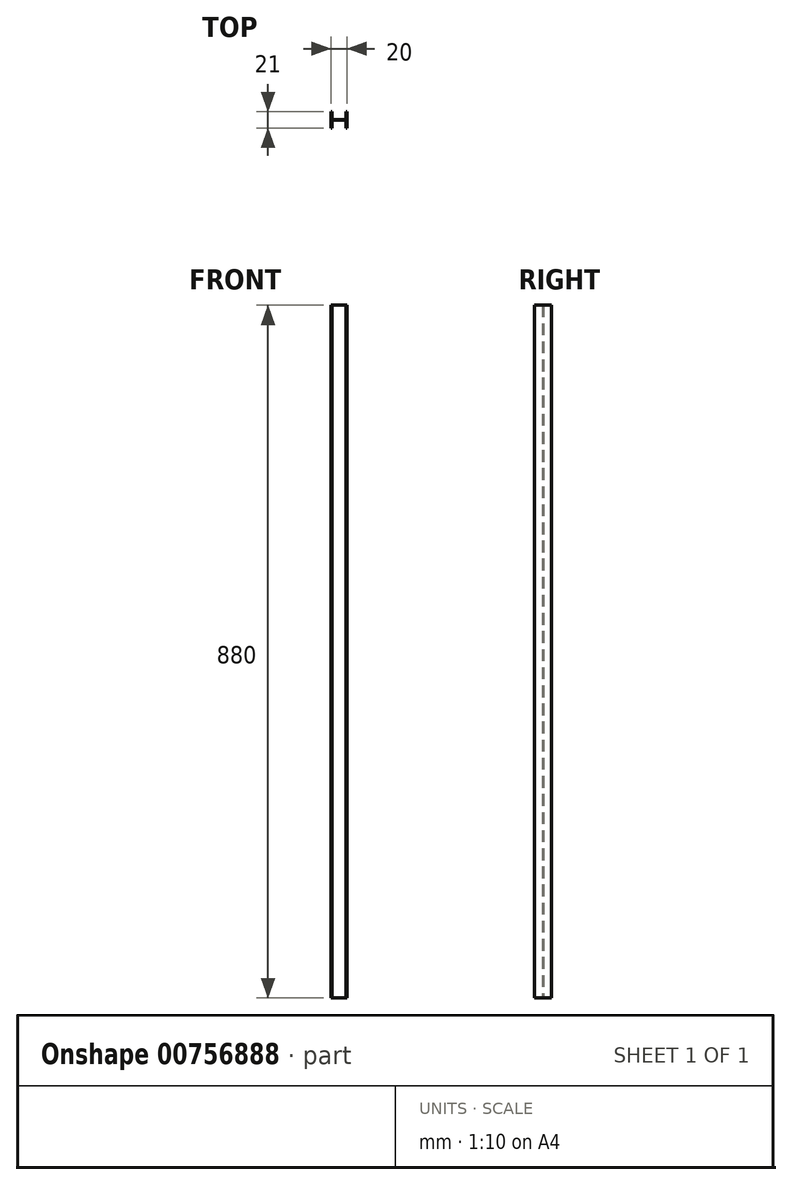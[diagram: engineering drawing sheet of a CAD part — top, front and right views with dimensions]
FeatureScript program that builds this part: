
annotation { "Feature Type Name" : "Feature", "Feature Type Description" : "" }
export const myFeature = defineFeature(function(context is Context, id is Id, definition is map)
    precondition{}
    {
        {
            var Q0;
            Q0=qCreatedBy(makeId("Top.planeOp"),FACE);
            var sketch = newSketch(context, id + "F0", { "sketchPlane" : qUnion([Q0])});
            skLineSegment(sketch, "E0.bottom", {"start": v(-5.8, 11) * mm, "end": v(-4.8, 11) * mm});
            skLineSegment(sketch, "E0.top", {"start": v(-5.8, -10) * mm, "end": v(-4.8, -10) * mm});
            skLineSegment(sketch, "E0.left", {"start": v(-5.8, 11) * mm, "end": v(-5.8, -10) * mm});
            skLineSegment(sketch, "E0.right", {"start": v(-4.8, 11) * mm, "end": v(-4.8, -10) * mm});
            skLineSegment(sketch, "E1.bottom", {"start": v(-4.8, 1) * mm, "end": v(13.2, 1) * mm});
            skLineSegment(sketch, "E1.top", {"start": v(-4.8, 0) * mm, "end": v(13.2, 0) * mm});
            skLineSegment(sketch, "E1.left", {"start": v(-4.8, 1) * mm, "end": v(-4.8, 0) * mm});
            skLineSegment(sketch, "E1.right", {"start": v(13.2, 1) * mm, "end": v(13.2, 0) * mm});
            skLineSegment(sketch, "E2.bottom", {"start": v(13.2, 11) * mm, "end": v(14.2, 11) * mm});
            skLineSegment(sketch, "E2.top", {"start": v(13.2, -10) * mm, "end": v(14.2, -10) * mm});
            skLineSegment(sketch, "E2.left", {"start": v(13.2, 11) * mm, "end": v(13.2, -10) * mm});
            skLineSegment(sketch, "E2.right", {"start": v(14.2, 11) * mm, "end": v(14.2, -10) * mm});
            skSolve(sketch);
        }
        {
            var Q0;
            Q0=qSketchRegion(id+"F0",true);
            extrude(context, id + "F1", {"entities" : qUnion([Q0]), "depth" : 880 * mm, "offsetDistance" : 25 * mm});
        }
    });
